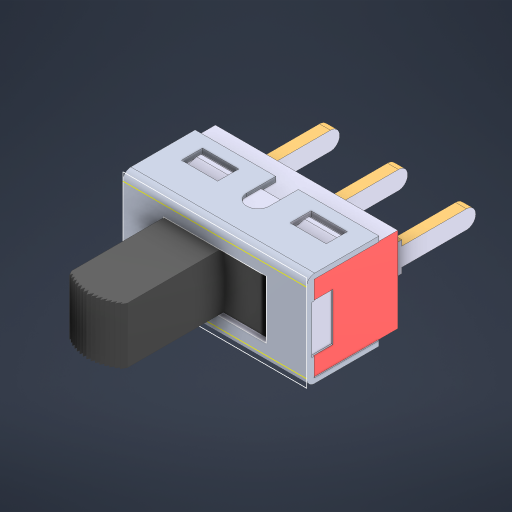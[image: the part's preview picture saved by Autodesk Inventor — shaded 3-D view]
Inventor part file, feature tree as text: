
AUTODESK INVENTOR PART (.ipt)
format: ipt  version: 2024 (Build 280153000, 153)  size: 492,032 bytes
history: native  units: in
note: dims shown in document units (in); Inventor stores cm internally (conversion verified against a paired STEP export)
features: sketch x1, projected_geometry x1, mirror x1
ambient origin geometry x8: Origin, YZ Plane, XZ Plane, XY Plane, X Axis, Y Axis, Z Axis, Center Point
bodies: Solid1 (feature_tree)
feature tree (3):
  sketch  "Sketch1"
  projected_geometry  "Projected Loop1"
  mirror  "Mirror1"
